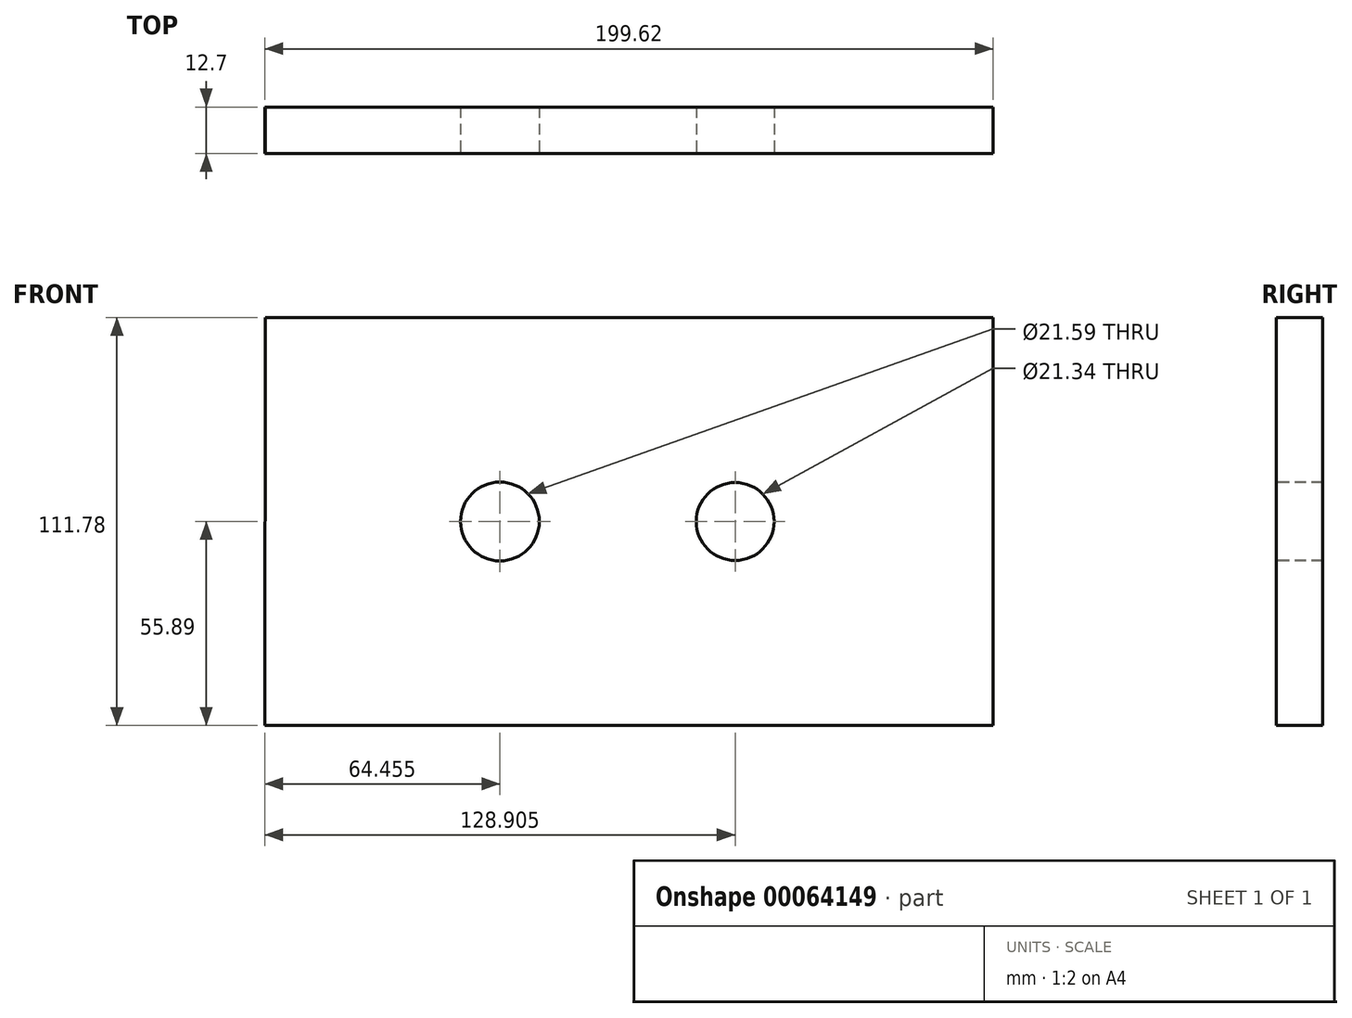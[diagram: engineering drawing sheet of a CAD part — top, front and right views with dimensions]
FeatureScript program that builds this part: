
annotation { "Feature Type Name" : "Feature", "Feature Type Description" : "" }
export const myFeature = defineFeature(function(context is Context, id is Id, definition is map)
    precondition{}
    {
        {
            var Q0;
            Q0=qCreatedBy(makeId("Front.planeOp"),FACE);
            var sketch = newSketch(context, id + "F0", { "sketchPlane" : qUnion([Q0])});
            skLineSegment(sketch, "E0", {"start": v(-99.62, 55.89) * mm, "end": v(99.8, 55.89) * mm});
            skLineSegment(sketch, "E1", {"start": v(99.8, 55.89) * mm, "end": v(99.8, -55.89) * mm});
            skLineSegment(sketch, "E2", {"start": v(99.8, -55.89) * mm, "end": v(-99.8, -55.89) * mm});
            skLineSegment(sketch, "E3", {"start": v(-99.8, -55.89) * mm, "end": v(-99.62, 55.89) * mm});
            skSolve(sketch);
        }
        {
            var Q0;
            Q0=makeQuery(id+"F0.imprint","IMPRINT",FACE,{"disambiguationData":[TD([[makeQuery(id+"F0.imprint","IMPRINT",EDGE,{"derivedFrom":sQuery(id+"F0.wireOp",EDGE,"E0")}),-1.0]])]});
            extrude(context, id + "F1", {"entities" : qUnion([Q0]), "depth" : 12.7 * mm});
        }
        {
            var Q0;
            Q0=makeQuery(id+"F1.opExtrude","CAP_FACE",FACE,{"disambiguationData":[OSD([sQuery(id+"F0.wireOp",EDGE,"E0"),sQuery(id+"F0.wireOp",EDGE,"E1"),sQuery(id+"F0.wireOp",EDGE,"E2"),sQuery(id+"F0.wireOp",EDGE,"E3")])],"isStart":false});
            var sketch = newSketch(context, id + "F2", { "sketchPlane" : qUnion([Q0])});
            skCircle(sketch, "E4", {"center": v(-35.35, 0) * mm, "radius": 10.87 * mm});
            skSolve(sketch);
        }
        {
            var Q0;
            Q0=sQuery(id+"F2.wireOp",VERTEX,"E4.center");
            var Q1;
            Q1=makeQuery(id+"F1.opExtrude","SWEPT_BODY",BODY,{"disambiguationData":[OSD([sQuery(id+"F0.wireOp",EDGE,"E0"),sQuery(id+"F0.wireOp",EDGE,"E1"),sQuery(id+"F0.wireOp",EDGE,"E2"),sQuery(id+"F0.wireOp",EDGE,"E3")])]});
            hole(context, id + "F3", {"style" : HoleStyle.SIMPLE, "holeDiameter" : 21.59 * mm, "endStyle" : HoleEndStyle.THROUGH, "locations" : qUnion([Q0]), "scope" : qUnion([Q1])});
        }
        {
            var Q0;
            Q0=makeQuery(id+"F1.opExtrude","CAP_FACE",FACE,{"disambiguationData":[OSD([sQuery(id+"F0.wireOp",EDGE,"E0"),sQuery(id+"F0.wireOp",EDGE,"E1"),sQuery(id+"F0.wireOp",EDGE,"E2"),sQuery(id+"F0.wireOp",EDGE,"E3")])],"isStart":false});
            var sketch = newSketch(context, id + "F4", { "sketchPlane" : qUnion([Q0])});
            skCircle(sketch, "E5", {"center": v(29.1, 0) * mm, "radius": 10.5 * mm});
            skSolve(sketch);
        }
        {
            var Q0;
            Q0=sQuery(id+"F4.wireOp",VERTEX,"E5.center");
            var Q1;
            Q1=makeQuery(id+"F1.opExtrude","SWEPT_BODY",BODY,{"disambiguationData":[OSD([sQuery(id+"F0.wireOp",EDGE,"E0"),sQuery(id+"F0.wireOp",EDGE,"E1"),sQuery(id+"F0.wireOp",EDGE,"E2"),sQuery(id+"F0.wireOp",EDGE,"E3")])]});
            hole(context, id + "F5", {"style" : HoleStyle.SIMPLE, "holeDiameter" : 21.34 * mm, "endStyle" : HoleEndStyle.THROUGH, "locations" : qUnion([Q0]), "scope" : qUnion([Q1])});
        }
    });
